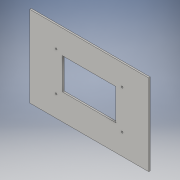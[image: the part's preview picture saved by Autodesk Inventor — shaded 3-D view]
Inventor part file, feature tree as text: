
AUTODESK INVENTOR PART (.ipt)
format: ipt  version: 2016 SP2 (Build 200236200, 236)  size: 116,736 bytes
history: native  units: in
note: dims shown in document units (in); Inventor stores cm internally (conversion verified against a paired STEP export)
features: sketch x3, extrude x2
ambient origin geometry x8: Origin, YZ Plane, XZ Plane, XY Plane, X Axis, Y Axis, Z Axis, Center Point
bodies: Solid1 (feature_tree)
feature tree (5):
  extrude  "Extrusion1"  Depth=5.9055in
  sketch  "Sketch2"  dims[d2=0.1181in d3=0.0in d7=0.126in]
  extrude  "Extrusion2"  Depth=0.1181in
  sketch  "Sketch1"  dims[d0=8.6614in d1=5.9055in]
  sketch  "Sketch3"  dims[d8=0.126in d9=0.126in d10=0.126in d11=3.8976in d12=2.2835in d13=0.4528in d14=0.1969in d15=0.3543in d16=0.126in d17=0.126in d18=0.126in d19=0.126in d20=3.8976in d21=2.2835in d22=0.4528in d23=0.1969in d24=0.3543in d25=0.1181in d26=0.0in]
